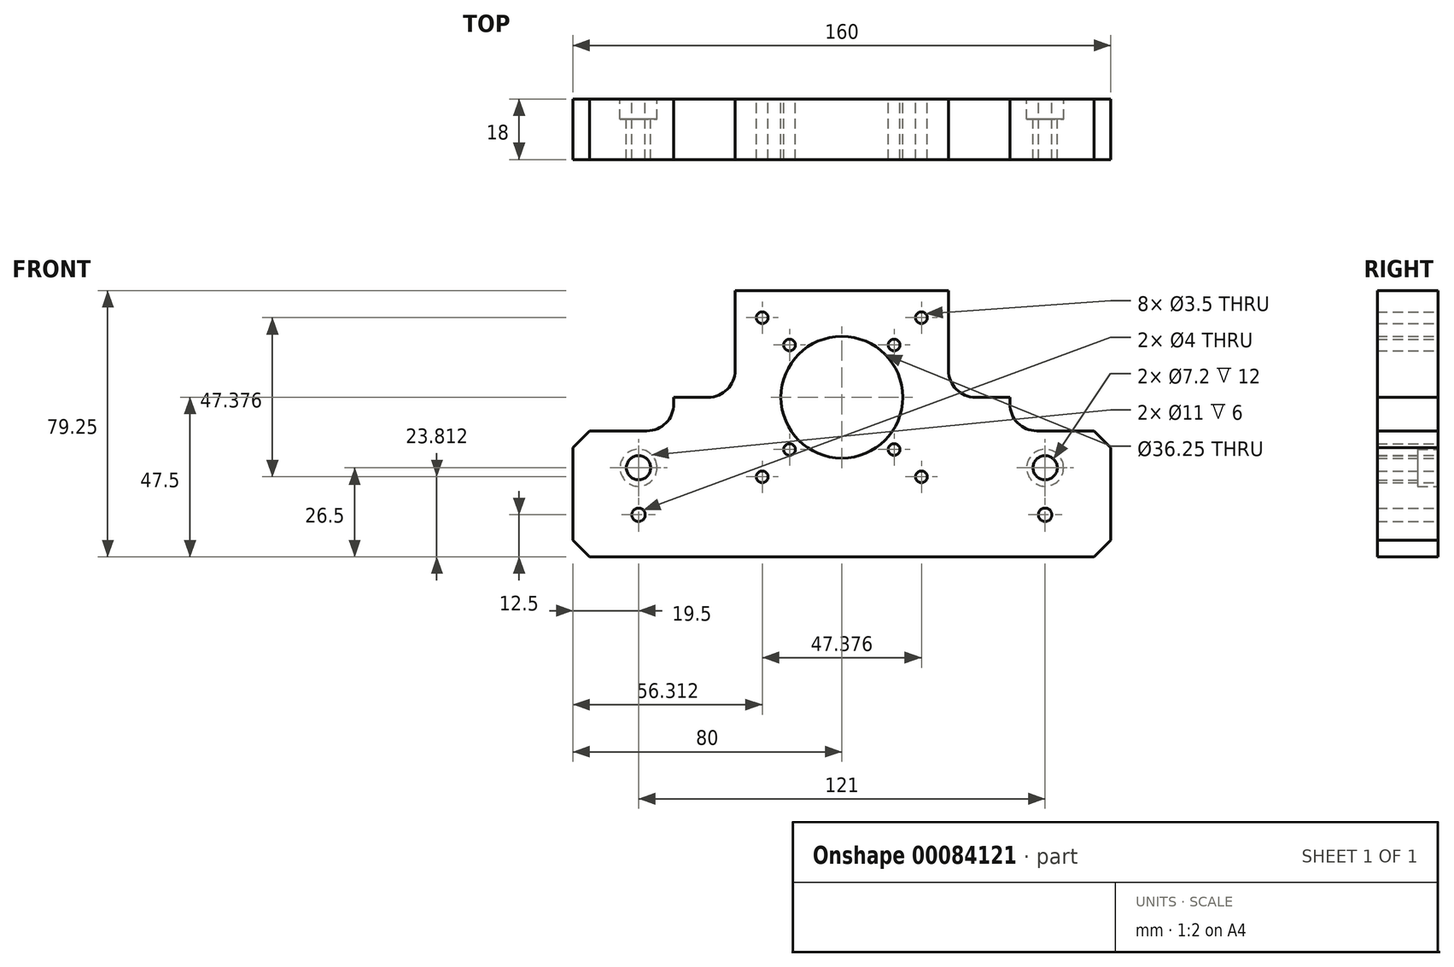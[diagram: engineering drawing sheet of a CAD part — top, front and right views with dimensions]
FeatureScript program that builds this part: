
annotation { "Feature Type Name" : "Feature", "Feature Type Description" : "" }
export const myFeature = defineFeature(function(context is Context, id is Id, definition is map)
    precondition{}
    {
        {
            var Q0;
            Q0=qCreatedBy(makeId("Front.planeOp"),FACE);
            var sketch = newSketch(context, id + "F0", { "sketchPlane" : qUnion([Q0])});
            skLineSegment(sketch, "E0.bottom", {"start": v(80, -33.75) * mm, "end": v(-80, -33.75) * mm});
            skLineSegment(sketch, "E0.top", {"start": v(80, 33.75) * mm, "end": v(-80, 33.75) * mm});
            skLineSegment(sketch, "E0.left", {"start": v(80, -33.75) * mm, "end": v(80, 33.75) * mm});
            skLineSegment(sketch, "E0.right", {"start": v(-80, -33.75) * mm, "end": v(-80, 33.75) * mm});
            skPoint(sketch, "E0.middle", {"position": v(0, 0) * mm});
            skPoint(sketch, "E1", {"position": v(-60.5, -33.75) * mm});
            skPoint(sketch, "E2", {"position": v(-80, 13.75) * mm});
            skPoint(sketch, "E3", {"position": v(-80, -7.25) * mm});
            skPoint(sketch, "E4", {"position": v(-80, -21.25) * mm});
            skPoint(sketch, "E5", {"position": v(0, -33.75) * mm});
            skPoint(sketch, "E6", {"position": v(0, 13.75) * mm});
            skCircle(sketch, "E7", {"center": v(0, 13.75) * mm, "radius": 18.12 * mm});
            skPoint(sketch, "E8", {"position": v(-60.5, -7.25) * mm});
            skPoint(sketch, "E9", {"position": v(-60.5, -21.25) * mm});
            skCircle(sketch, "E10", {"center": v(-60.5, -21.25) * mm, "radius": 2 * mm});
            skCircle(sketch, "E11.MirrorC", {"center": v(60.5, -21.25) * mm, "radius": 2 * mm});
            skCircle(sketch, "E12", {"center": v(0, 13.75) * mm, "radius": 22 * mm, "construction": true});
            skLineSegment(sketch, "E13", {"start": v(0, 13.75) * mm, "end": v(15.56, -1.8) * mm, "construction": true});
            skCircle(sketch, "E14", {"center": v(15.56, -1.8) * mm, "radius": 1.75 * mm});
            skCircle(sketch, "E15.1.0", {"center": v(15.56, 29.3) * mm, "radius": 1.75 * mm});
            skCircle(sketch, "E15.2.0", {"center": v(-15.56, 29.3) * mm, "radius": 1.75 * mm});
            skCircle(sketch, "E15.3.0", {"center": v(-15.56, -1.8) * mm, "radius": 1.75 * mm});
            skLineSegment(sketch, "E16.bottom", {"start": v(31.75, -18) * mm, "end": v(-31.75, -18) * mm, "construction": true});
            skLineSegment(sketch, "E16.top", {"start": v(31.75, 45.5) * mm, "end": v(-31.75, 45.5) * mm});
            skLineSegment(sketch, "E16.left", {"start": v(31.75, -18) * mm, "end": v(31.75, 45.5) * mm, "construction": true});
            skLineSegment(sketch, "E16.right", {"start": v(-31.75, -18) * mm, "end": v(-31.75, 45.5) * mm, "construction": true});
            skLineSegment(sketch, "E17", {"start": v(-80, 33.75) * mm, "end": v(-31.75, 45.5) * mm});
            skLineSegment(sketch, "E18", {"start": v(31.75, 45.5) * mm, "end": v(80, 33.75) * mm});
            skLineSegment(sketch, "E19", {"start": v(-31.75, 45.5) * mm, "end": v(-31.75, 13.75) * mm});
            skLineSegment(sketch, "E20", {"start": v(-31.75, 13.75) * mm, "end": v(-80, 13.75) * mm});
            skLineSegment(sketch, "E21", {"start": v(31.75, 45.5) * mm, "end": v(31.75, 13.75) * mm});
            skLineSegment(sketch, "E22", {"start": v(31.75, 13.75) * mm, "end": v(80, 13.75) * mm});
            skCircle(sketch, "E23", {"center": v(0, 13.75) * mm, "radius": 33.5 * mm, "construction": true});
            skLineSegment(sketch, "E24", {"start": v(0, 13.75) * mm, "end": v(-31.75, 45.5) * mm, "construction": true});
            skCircle(sketch, "E25", {"center": v(-23.69, 37.44) * mm, "radius": 1.75 * mm});
            skCircle(sketch, "E26.1.0", {"center": v(-23.69, -9.94) * mm, "radius": 1.75 * mm});
            skLineSegment(sketch, "E26.1.1", {"start": v(-31.75, 45.5) * mm, "end": v(-31.75, -18) * mm});
            skCircle(sketch, "E26.2.0", {"center": v(23.69, -9.94) * mm, "radius": 1.75 * mm});
            skLineSegment(sketch, "E26.2.1", {"start": v(-31.75, -18) * mm, "end": v(31.75, -18) * mm});
            skCircle(sketch, "E26.3.0", {"center": v(23.69, 37.44) * mm, "radius": 1.75 * mm});
            skLineSegment(sketch, "E26.3.1", {"start": v(31.75, -18) * mm, "end": v(31.75, 45.5) * mm});
            skPoint(sketch, "E27.MirrorP", {"position": v(60.5, -7.25) * mm});
            skLineSegment(sketch, "E28", {"start": v(-80, 3.75) * mm, "end": v(-50, 3.75) * mm});
            skLineSegment(sketch, "E29", {"start": v(-50, 3.75) * mm, "end": v(-50, 13.75) * mm});
            skLineSegment(sketch, "E30.MirrorCS", {"start": v(80, 3.75) * mm, "end": v(50, 3.75) * mm});
            skLineSegment(sketch, "E31.MirrorCS", {"start": v(50, 3.75) * mm, "end": v(50, 13.75) * mm});
            skSolve(sketch);
        }
        {
            var Q0;
            {var subQ1=sQuery(id+"F0.wireOp",EDGE,"E0.bottom");Q0=makeQuery(id+"F0.imprint","IMPRINT",FACE,{"disambiguationData":[TD([[makeQuery(id+"F0.imprint","IMPRINT",EDGE,{"derivedFrom":subQ1}),-1.0]])]});}
            var Q1;
            {var subQ5=sQuery(id+"F0.wireOp",EDGE,"E16.top");Q1=makeQuery(id+"F0.imprint","IMPRINT",FACE,{"disambiguationData":[TD([[makeQuery(id+"F0.imprint","IMPRINT",EDGE,{"derivedFrom":subQ5}),1.0]])]});}
            var Q2;
            Q2=makeQuery(id+"F0.imprint","IMPRINT",FACE,{"disambiguationData":[TD([[makeQuery(id+"F0.imprint","IMPRINT",EDGE,{"derivedFrom":sQuery(id+"F0.wireOp",EDGE,"E7")}),-1.0]])]});
            extrude(context, id + "F1", {"entities" : qUnion([Q0, Q1, Q2]), "depth" : 18 * mm});
        }
        {
            var Q0;
            Q0=makeQuery(id+"F1.opExtrude","SWEPT_EDGE",EDGE,{"disambiguationData":[OSD([sQuery(id+"F0.wireOp",EDGE,"E0.bottom"),sQuery(id+"F0.wireOp",EDGE,"E0.right")])]});
            var Q1;
            Q1=makeQuery(id+"F1.opExtrude","SWEPT_EDGE",EDGE,{"disambiguationData":[OSD([sQuery(id+"F0.wireOp",EDGE,"E0.bottom"),sQuery(id+"F0.wireOp",EDGE,"E0.left")])]});
            var Q2;
            Q2=makeQuery(id+"F1.opExtrude","SWEPT_EDGE",EDGE,{"disambiguationData":[OSD([sQuery(id+"F0.wireOp",EDGE,"E0.left"),sQuery(id+"F0.wireOp",EDGE,"koAOt2NU-ont5-5yzo-7Uvz-TOEI61CWz3w5")])]});
            var Q3;
            Q3=makeQuery(id+"F1.opExtrude","SWEPT_EDGE",EDGE,{"disambiguationData":[OSD([sQuery(id+"F0.wireOp",EDGE,"E0.right"),sQuery(id+"F0.wireOp",EDGE,"2b075610-e8f6-4bec-89b8-de3a2f93d7d90.MirrorCS")])]});
            chamfer(context, id + "F2", {"entities" : qUnion([Q0, Q1, Q2, Q3]), "width" : 5 * mm, "tangentPropagation" : true});
        }
        {
            var Q0;
            Q0=makeQuery(id+"F1.opExtrude","SWEPT_EDGE",EDGE,{"disambiguationData":[OSD([sQuery(id+"F0.wireOp",EDGE,"E22"),sQuery(id+"F0.wireOp",EDGE,"E26.3.1")])]});
            var Q1;
            Q1=makeQuery(id+"F1.opExtrude","SWEPT_EDGE",EDGE,{"disambiguationData":[OSD([sQuery(id+"F0.wireOp",EDGE,"E20"),sQuery(id+"F0.wireOp",EDGE,"E26.1.1")])]});
            var Q2;
            Q2=makeQuery(id+"F1.opExtrude","SWEPT_EDGE",EDGE,{"disambiguationData":[OSD([sQuery(id+"F0.wireOp",EDGE,"E30.MirrorCS"),sQuery(id+"F0.wireOp",EDGE,"E31.MirrorCS")])]});
            var Q3;
            Q3=makeQuery(id+"F1.opExtrude","SWEPT_EDGE",EDGE,{"disambiguationData":[OSD([sQuery(id+"F0.wireOp",EDGE,"E28"),sQuery(id+"F0.wireOp",EDGE,"E29")])]});
            fillet(context, id + "F3", {"entities" : qUnion([Q0, Q1, Q2, Q3]), "radius" : 8 * mm, "tangentPropagation" : true, "allowEdgeOverflow" : false});
        }
        {
            var Q0;
            Q0=sQuery(id+"F0.wireOp",VERTEX,"E27.MirrorP");
            var Q1;
            Q1=sQuery(id+"F0.wireOp",VERTEX,"E8");
            var Q2;
            Q2=makeQuery(id+"F1.opExtrude","SWEPT_BODY",BODY,{"disambiguationData":[OSD([sQuery(id+"F0.wireOp",EDGE,"E0.bottom"),sQuery(id+"F0.wireOp",EDGE,"E0.left"),sQuery(id+"F0.wireOp",EDGE,"E0.right"),sQuery(id+"F0.wireOp",EDGE,"E7"),sQuery(id+"F0.wireOp",EDGE,"E10"),sQuery(id+"F0.wireOp",EDGE,"E11.MirrorC"),sQuery(id+"F0.wireOp",EDGE,"E14"),sQuery(id+"F0.wireOp",EDGE,"E15.1.0"),sQuery(id+"F0.wireOp",EDGE,"E15.2.0"),sQuery(id+"F0.wireOp",EDGE,"E15.3.0"),sQuery(id+"F0.wireOp",EDGE,"E16.top"),sQuery(id+"F0.wireOp",EDGE,"E20"),sQuery(id+"F0.wireOp",EDGE,"E22"),sQuery(id+"F0.wireOp",EDGE,"E25"),sQuery(id+"F0.wireOp",EDGE,"E26.1.0"),sQuery(id+"F0.wireOp",EDGE,"E26.1.1"),sQuery(id+"F0.wireOp",EDGE,"E26.2.0"),sQuery(id+"F0.wireOp",EDGE,"E26.3.0"),sQuery(id+"F0.wireOp",EDGE,"E26.3.1")])]});
            hole(context, id + "F4", {"style" : HoleStyle.C_BORE, "endStyle" : HoleEndStyle.BLIND, "oppositeDirection" : true, "holeDiameter" : 7.2 * mm, "cBoreDiameter" : 11 * mm, "cBoreDepth" : 6 * mm, "holeDepth" : 35 * mm, "startFromSketch" : true, "locations" : qUnion([Q0, Q1]), "scope" : qUnion([Q2])});
        }
    });
